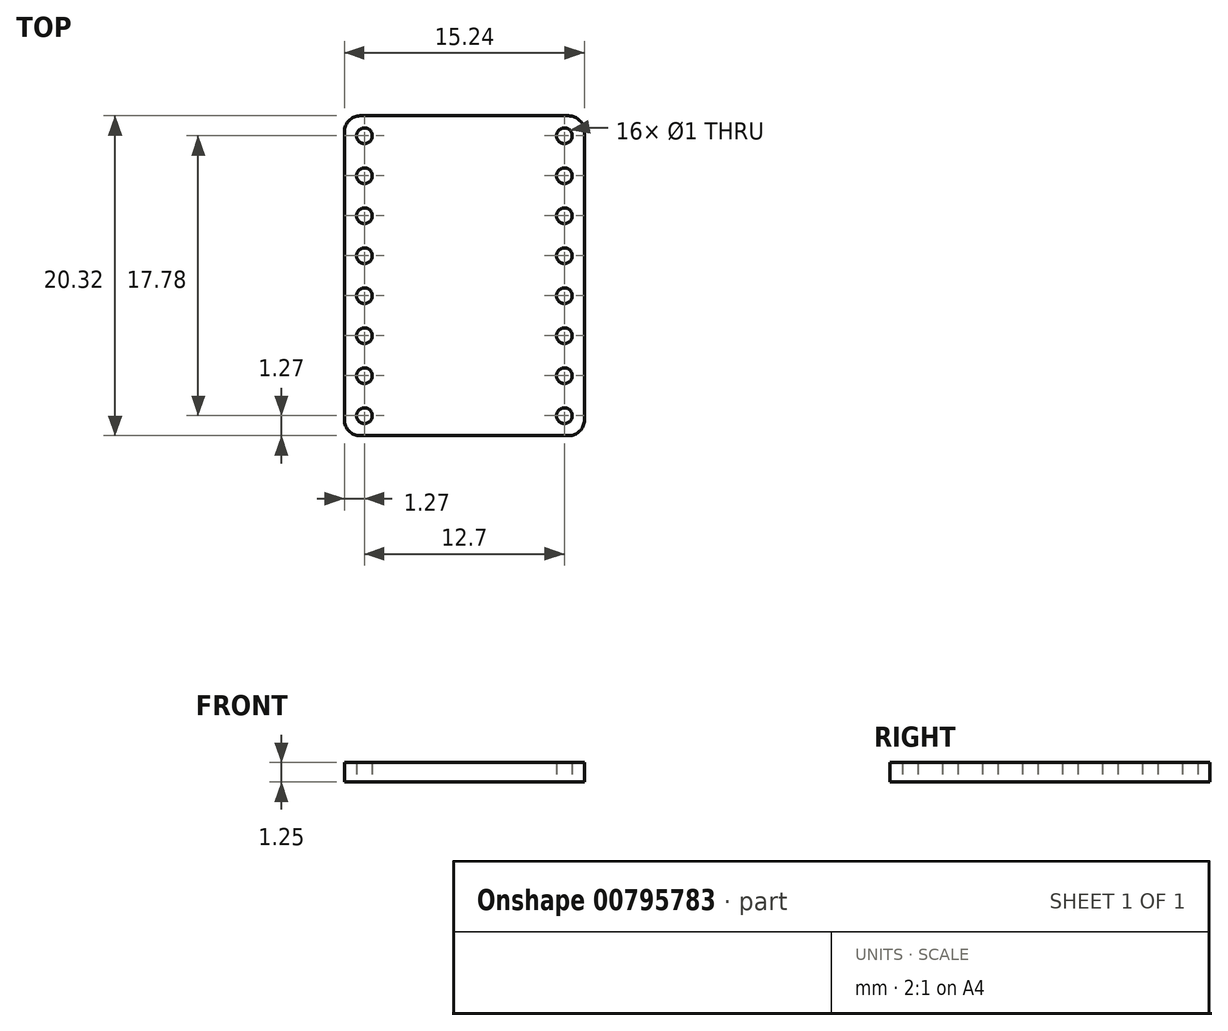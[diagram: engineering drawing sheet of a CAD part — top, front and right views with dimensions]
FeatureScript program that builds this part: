
annotation { "Feature Type Name" : "Feature", "Feature Type Description" : "" }
export const myFeature = defineFeature(function(context is Context, id is Id, definition is map)
    precondition{}
    {
        {
            var Q0;
            Q0=qCreatedBy(makeId("Top.planeOp"),FACE);
            var sketch = newSketch(context, id + "F0", { "sketchPlane" : qUnion([Q0])});
            skLineSegment(sketch, "E0.bottom", {"start": v(7.62, -10.16) * mm, "end": v(-7.62, -10.16) * mm});
            skLineSegment(sketch, "E0.top", {"start": v(7.62, 10.16) * mm, "end": v(-7.62, 10.16) * mm});
            skLineSegment(sketch, "E0.left", {"start": v(7.62, -10.16) * mm, "end": v(7.62, 10.16) * mm});
            skLineSegment(sketch, "E0.right", {"start": v(-7.62, -10.16) * mm, "end": v(-7.62, 10.16) * mm});
            skLineSegment(sketch, "E1", {"start": v(6.35, 10.16) * mm, "end": v(6.35, -10.16) * mm, "construction": true});
            skCircle(sketch, "E2", {"center": v(6.35, 6.35) * mm, "radius": 0.5 * mm});
            skCircle(sketch, "E3", {"center": v(6.35, 3.8) * mm, "radius": 0.5 * mm});
            skCircle(sketch, "E4", {"center": v(6.35, 1.27) * mm, "radius": 0.5 * mm});
            skCircle(sketch, "E5", {"center": v(6.35, -1.27) * mm, "radius": 0.5 * mm});
            skCircle(sketch, "E6", {"center": v(6.35, -3.81) * mm, "radius": 0.5 * mm});
            skCircle(sketch, "E7", {"center": v(6.35, -6.35) * mm, "radius": 0.5 * mm});
            skCircle(sketch, "E8", {"center": v(6.35, -8.9) * mm, "radius": 0.5 * mm});
            skCircle(sketch, "E9", {"center": v(6.35, 8.89) * mm, "radius": 0.5 * mm});
            skLineSegment(sketch, "E10", {"start": v(-6.35, 10.16) * mm, "end": v(-6.35, -10.16) * mm, "construction": true});
            skCircle(sketch, "E11", {"center": v(-6.35, 6.35) * mm, "radius": 0.5 * mm});
            skCircle(sketch, "E12", {"center": v(-6.35, 3.8) * mm, "radius": 0.5 * mm});
            skCircle(sketch, "E13", {"center": v(-6.35, 1.27) * mm, "radius": 0.5 * mm});
            skCircle(sketch, "E14", {"center": v(-6.35, -1.27) * mm, "radius": 0.5 * mm});
            skCircle(sketch, "E15", {"center": v(-6.35, -3.81) * mm, "radius": 0.5 * mm});
            skCircle(sketch, "E16", {"center": v(-6.35, -6.35) * mm, "radius": 0.5 * mm});
            skCircle(sketch, "E17", {"center": v(-6.35, -8.9) * mm, "radius": 0.5 * mm});
            skCircle(sketch, "E18", {"center": v(-6.35, 8.89) * mm, "radius": 0.5 * mm});
            skSolve(sketch);
        }
        {
            var Q0;
            Q0=makeQuery(id+"F0.imprint","IMPRINT",FACE,{"disambiguationData":[TD([[makeQuery(id+"F0.imprint","IMPRINT",EDGE,{"derivedFrom":sQuery(id+"F0.wireOp",EDGE,"E0.bottom")}),-1.0]])]});
            extrude(context, id + "F1", {"entities" : qUnion([Q0]), "depth" : 1.25 * mm, "offsetDistance" : 25 * mm});
        }
        {
            var Q0;
            Q0=makeQuery(id+"F1.opExtrude","SWEPT_EDGE",EDGE,{"disambiguationData":[OSD([sQuery(id+"F0.wireOp",EDGE,"E0.top"),sQuery(id+"F0.wireOp",EDGE,"E0.right")])]});
            var Q1;
            Q1=makeQuery(id+"F1.opExtrude","SWEPT_EDGE",EDGE,{"disambiguationData":[OSD([sQuery(id+"F0.wireOp",EDGE,"E0.bottom"),sQuery(id+"F0.wireOp",EDGE,"E0.right")])]});
            var Q2;
            Q2=makeQuery(id+"F1.opExtrude","SWEPT_EDGE",EDGE,{"disambiguationData":[OSD([sQuery(id+"F0.wireOp",EDGE,"E0.bottom"),sQuery(id+"F0.wireOp",EDGE,"E0.left")])]});
            var Q3;
            Q3=makeQuery(id+"F1.opExtrude","SWEPT_EDGE",EDGE,{"disambiguationData":[OSD([sQuery(id+"F0.wireOp",EDGE,"E0.top"),sQuery(id+"F0.wireOp",EDGE,"E0.left")])]});
            fillet(context, id + "F2", {"entities" : qUnion([Q0, Q1, Q2, Q3]), "radius" : 1 * mm, "tangentPropagation" : true, "allowEdgeOverflow" : false});
        }
    });
